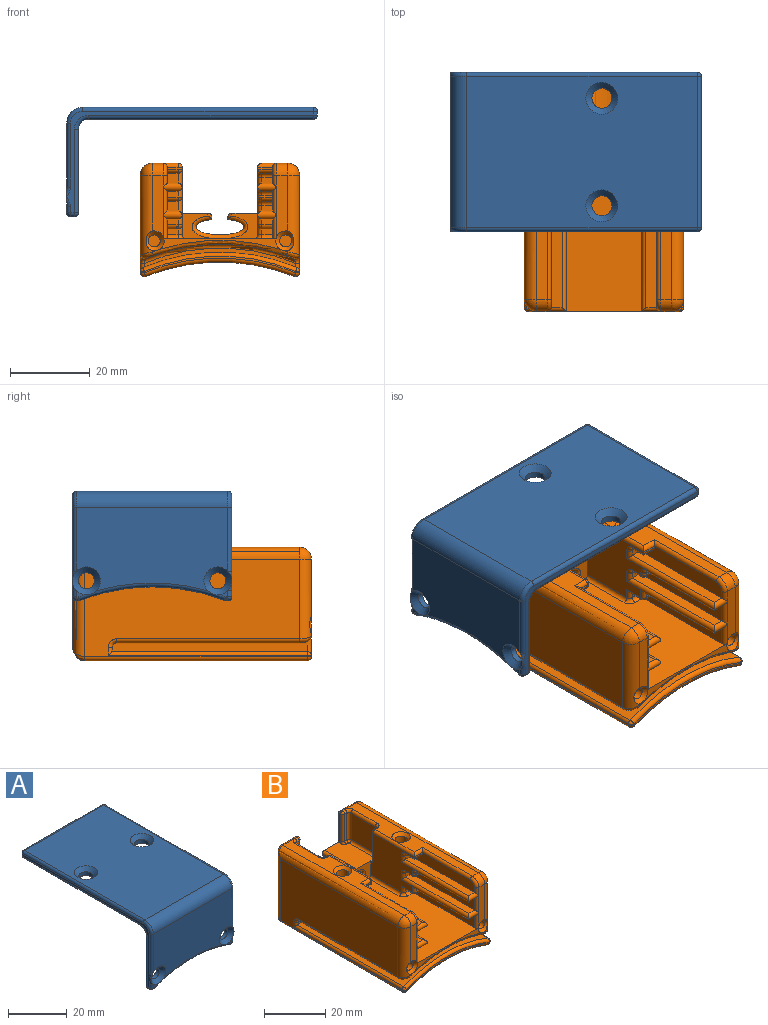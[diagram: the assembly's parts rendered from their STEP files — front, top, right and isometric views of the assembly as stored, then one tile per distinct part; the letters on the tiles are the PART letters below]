
ASSEMBLY  parts=2 mates=1
PART A: 66 faces, bbox 40.9x63.5x28 mm
  f0: plane 1.91x1.55mm, normal (0,-1,0), area 1.3mm2, adj f6,f26,f34,f58
  f1: plane 38x20.96mm, normal (0,-1,0), area 696.7mm2, adj f16,f25,f26,f29,f44,f58
  f2: plane 1.91x1.55mm, normal (0,-1,0), area 1.3mm2, adj f3,f25,f49,f58
  f3: cylinder r=1mm len=1mm, axis (-1,0,0), area 0.7mm2, adj f2,f7,f51,f59
  f4: plane 1x0.43mm, normal (0,0,-1), area 0.4mm2, adj f6,f8,f38,f62
  f5: cylinder r=1mm len=1mm, axis (-1,0,0), area 0.7mm2, adj f7,f9,f55,f63
  f6: cylinder r=1mm len=1mm, axis (-1,0,0), area 0.7mm2, adj f0,f4,f36,f60
  f7: plane 1x0.43mm, normal (0,0,-1), area 0.4mm2, adj f3,f5,f53,f61
  f8: cylinder r=1mm len=1mm, axis (-1,0,0), area 0.7mm2, adj f4,f9,f40,f64
  f9: plane 38x21mm, normal (0,1,0), area 685.6mm2, adj f5,f8,f10,f21,f22,f42,f57,f65
  f10: cylinder r=2.5mm len=38mm, axis (-1,0,0), area 149.2mm2, adj f9,f11,f41,f56
  f11: plane 56.5x38mm, normal (0,0,-1), area 2107.7mm2, adj f10,f12,f19,f20,f39,f54
  f12: cylinder r=1mm len=38mm, axis (-1,0,0), area 59.7mm2, adj f11,f13,f37,f52
  f13: plane 38x1mm, normal (0,1,0), area 38mm2, adj f12,f14,f35,f50
  f14: cylinder r=1mm len=38mm, axis (-1,0,0), area 59.7mm2, adj f13,f15,f33,f48
  f15: plane 58x38mm, normal (0,0,1), area 2103.5mm2, adj f14,f16,f23,f24,f31,f46
  f16: cylinder r=4mm len=38mm, axis (-1,0,0), area 238.8mm2, adj f1,f15,f30,f45
  f17: plane 62.13x25.63mm, normal (1,0,0), area 88mm2, adj f43,f44,f45,f46,f47,f49,f50,f53
  f18: plane 62.13x25.63mm, normal (-1,0,0), area 88mm2, adj f28,f29,f30,f31,f32,f34,f35,f38
  f19: cylinder r=2.5mm len=5mm, axis (0,0,1), area 23.6mm2, adj f11,f24
  f20: cylinder r=2.5mm len=5mm, axis (0,0,1), area 23.6mm2, adj f11,f23
  f21: cylinder r=2mm len=4mm, axis (0,1,0), area 18.8mm2, adj f9,f26
  f22: cylinder r=2mm len=4mm, axis (0,1,0), area 18.8mm2, adj f9,f25
  f23: cone r=2.5mm half-angle=45deg, axis (0,0,1), area 43.3mm2, adj f15,f20
  f24: cone r=2.5mm half-angle=45deg, axis (0,0,1), area 43.3mm2, adj f15,f19
  f25: cone r=3.5mm half-angle=45deg, axis (0,-1,0), area 36.7mm2, adj f1,f2,f22,f43,f47,f58
  f26: cone r=3.5mm half-angle=45deg, axis (0,-1,0), area 36.7mm2, adj f0,f1,f21,f28,f32,f58
  f27: cylinder r=50mm len=36.41mm, axis (0,-1,0), area 37.3mm2, adj f58,f61,f62,f65
  f28: bspline ~2.56x1.07mm, area 1.7mm2, adj f18,f26,f29
  f29: cylinder r=1mm len=16.05mm, axis (0,0,-1), area 25.2mm2, adj f1,f18,f28,f30
  f30: torus R=3mm, axis (1,0,0), area 9mm2, adj f16,f18,f29,f31
  f31: cylinder r=1mm len=58mm, axis (0,-1,0), area 91.1mm2, adj f15,f18,f30,f33
  f32: bspline ~2.56x1.07mm, area 1.7mm2, adj f18,f26,f34
  f33: sphere r=1mm, area 1.6mm2, adj f14,f31,f35
  f34: cylinder r=1mm len=1.55mm, axis (0,0,-1), area 2.4mm2, adj f0,f18,f32,f36
  f35: cylinder r=1mm len=1mm, axis (0,0,1), area 1.6mm2, adj f13,f18,f33,f37
  f36: sphere r=1mm, area 1.6mm2, adj f6,f34,f38
  f37: sphere r=1mm, area 1.6mm2, adj f12,f35,f39
  f38: cylinder r=1mm len=1mm, axis (0,1,0), area 1.6mm2, adj f4,f18,f36,f40
  f39: cylinder r=1mm len=56.5mm, axis (0,1,0), area 88.7mm2, adj f11,f18,f37,f41
  f40: sphere r=1mm, area 1.6mm2, adj f8,f38,f42
  f41: torus R=3.5mm, axis (1,0,0), area 7.1mm2, adj f10,f18,f39,f42
  f42: cylinder r=1mm len=21mm, axis (0,0,1), area 33mm2, adj f9,f18,f40,f41
  f43: bspline ~2.56x1.07mm, area 1.7mm2, adj f17,f25,f44
  f44: cylinder r=1mm len=16.05mm, axis (0,0,1), area 25.2mm2, adj f1,f17,f43,f45
  f45: torus R=3mm, axis (1,0,0), area 9mm2, adj f16,f17,f44,f46
  f46: cylinder r=1mm len=58mm, axis (0,1,0), area 91.1mm2, adj f15,f17,f45,f48
  f47: bspline ~2.56x1.07mm, area 1.7mm2, adj f17,f25,f49
  f48: sphere r=1mm, area 1.6mm2, adj f14,f46,f50
  f49: cylinder r=1mm len=1.55mm, axis (0,0,1), area 2.4mm2, adj f2,f17,f47,f51
  f50: cylinder r=1mm len=1mm, axis (0,0,-1), area 1.6mm2, adj f13,f17,f48,f52
  f51: sphere r=1mm, area 1.6mm2, adj f3,f49,f53
  f52: sphere r=1mm, area 1.6mm2, adj f12,f50,f54
  f53: cylinder r=1mm len=1mm, axis (0,-1,0), area 1.6mm2, adj f7,f17,f51,f55
  f54: cylinder r=1mm len=56.5mm, axis (0,-1,0), area 88.7mm2, adj f11,f17,f52,f56
  f55: sphere r=1mm, area 1.6mm2, adj f5,f53,f57
  f56: torus R=3.5mm, axis (1,0,0), area 7.1mm2, adj f10,f17,f54,f57
  f57: cylinder r=1mm len=21mm, axis (0,0,-1), area 33mm2, adj f9,f17,f55,f56
  f58: torus R=51mm, axis (0,1,0), area 57.3mm2, adj f0,f1,f2,f25,f26,f27,f59,f60
  f59: sphere r=1mm, area 0.4mm2, adj f3,f58,f61
  f60: sphere r=1mm, area 0.4mm2, adj f6,f58,f62
  f61: cylinder r=1mm len=1mm, axis (0,-1,0), area 0.4mm2, adj f7,f27,f59,f63
  f62: cylinder r=1mm len=1mm, axis (0,-1,0), area 0.4mm2, adj f4,f27,f60,f64
  f63: sphere r=1mm, area 0.4mm2, adj f5,f61,f65
  f64: sphere r=1mm, area 0.4mm2, adj f8,f62,f65
  f65: torus R=51mm, axis (0,-1,0), area 59mm2, adj f9,f27,f63,f64
PART B: 210 faces, bbox 44.8x60.6x29.6 mm
  f0: plane 15.41x2.75mm, normal (0,-1,0), area 39.4mm2, adj f65,f66,f122,f135,f139,f196
  f1: plane 30.46x2.65mm, normal (0,-1,0), area 28.4mm2, adj f43,f98,f196,f197
  f2: plane 0.74x0.29mm, normal (0,-1,0), area 0.1mm2, adj f73,f98,f197
  f3: plane 0.74x0.29mm, normal (0,-1,0), area 0.1mm2, adj f66,f98,f196
  f4: plane 9.5x6.5mm, normal (0,-1,0), area 26mm2, adj f5,f43,f52,f141,f187,f188
  f5: plane 16.37x8.87mm, normal (0,0,1), area 122.3mm2, adj f4,f6,f52,f55,f58,f142,f148,f161
  f6: plane 34x23.63mm, normal (0,1,0), area 451.1mm2, adj f5,f58,f59,f61,f69,f70,f71,f102
  f7: plane 9.5x6.5mm, normal (0,-1,0), area 26mm2, adj f43,f51,f61,f100,f186,f187
  f8: plane 56x6.5mm, normal (0,0,1), area 206.2mm2, adj f65,f68,f102,f105,f108,f112,f114,f123
  f9: plane 56x6.5mm, normal (0,0,1), area 206.2mm2, adj f72,f75,f146,f149,f153,f155,f162,f174
  f10: plane 4x2.75mm, normal (0,0,-1), area 11mm2, adj f15,f34,f124,f130
  f11: plane 4x2.75mm, normal (0,0,-1), area 11mm2, adj f17,f38,f118,f119
  f12: plane 4x2.75mm, normal (0,0,-1), area 11mm2, adj f18,f42,f110,f111
  f13: plane 15.41x2.75mm, normal (0,-1,0), area 39.4mm2, adj f73,f75,f163,f178,f184,f197
  f14: plane 29x2.75mm, normal (0,0,1), area 79.7mm2, adj f15,f34,f134,f137
  f15: plane 2.75x2.5mm, normal (0,-1,0), area 6.9mm2, adj f10,f14,f34,f133
  f16: plane 29x2.75mm, normal (0,0,1), area 79.7mm2, adj f17,f38,f121,f128
  f17: plane 2.75x2.5mm, normal (0,-1,0), area 6.9mm2, adj f11,f16,f38,f120
  f18: plane 2.75x1.5mm, normal (0,-1,0), area 4.1mm2, adj f12,f42,f101,f107
  f19: plane 24x2.75mm, normal (0,0,-1), area 66mm2, adj f20,f42,f121,f128
  f20: plane 2.75x1.5mm, normal (0,-1,0), area 4.1mm2, adj f19,f42,f111,f116
  f21: plane 24x2.75mm, normal (0,0,-1), area 66mm2, adj f22,f38,f134,f137
  f22: plane 2.75x1.5mm, normal (0,-1,0), area 4.1mm2, adj f21,f38,f119,f131
  f23: plane 2.75x0.5mm, normal (0,-1,0), area 1.4mm2, adj f34,f124,f125,f132
  f24: plane 3x2.75mm, normal (0,0,-1), area 8.3mm2, adj f36,f167,f172,f173
  f25: plane 3x2.75mm, normal (0,0,-1), area 8.3mm2, adj f40,f157,f159,f160
  f26: plane 4x2.75mm, normal (0,0,-1), area 11mm2, adj f44,f45,f150,f151
  f27: plane 56x24.5mm, normal (1,0,0), area 1124.7mm2, adj f71,f72,f73,f80,f85,f90,f92,f95
  f28: plane 38x4.17mm, normal (0,-1,0), area 17mm2, adj f81,f82,f85,f86
  f29: plane 56x24.5mm, normal (-1,0,0), area 1124.7mm2, adj f66,f68,f69,f77,f82,f87,f89,f91
  f30: cylinder r=50mm len=56mm, axis (0,1,0), area 2137.8mm2, adj f70,f77,f80,f81
  f31: cylinder r=50mm len=49.08mm, axis (0,-1,0), area 1951.2mm2, adj f33,f86,f87,f89,f90,f92
  f32: cylinder r=50mm len=48mm, axis (0,-1,0), area 1802.3mm2, adj f93,f94,f96,f97,f98,f99,f190,f191
  f33: plane 38x4.75mm, normal (0,-1,0), area 37mm2, adj f31,f89,f92,f93
  f34: plane 29x4mm, normal (1,0,0), area 107.9mm2, adj f10,f14,f15,f23,f124,f136,f138,f139
  f35: plane 29x2.75mm, normal (0,0,1), area 79.7mm2, adj f36,f37,f179,f182
  f36: plane 29x4mm, normal (-1,0,0), area 107.6mm2, adj f24,f35,f37,f50,f167,f173,f181,f183
  f37: plane 2.75x1.5mm, normal (0,-1,0), area 4.1mm2, adj f35,f36,f173,f180
  f38: plane 29x5mm, normal (1,0,0), area 132.7mm2, adj f11,f16,f17,f21,f22,f119,f135
  f39: plane 29x2.75mm, normal (0,0,1), area 79.7mm2, adj f40,f41,f164,f169
  f40: plane 29x5mm, normal (-1,0,0), area 132.3mm2, adj f25,f39,f41,f48,f49,f157,f159,f170
  f41: plane 2.75x1.5mm, normal (0,-1,0), area 4.1mm2, adj f39,f40,f157,f165
  f42: plane 29x5mm, normal (1,0,0), area 132.5mm2, adj f12,f18,f19,f20,f43,f101,f111,f122
  f43: plane 45x28.14mm, normal (0,0,1), area 1042.6mm2, adj f1,f4,f7,f42,f44,f100,f101,f104
  f44: plane 29x5mm, normal (-1,0,0), area 132.5mm2, adj f26,f43,f45,f46,f47,f140,f150,f163
  f45: plane 2.75x1.5mm, normal (0,-1,0), area 4.1mm2, adj f26,f44,f140,f147
  f46: plane 24x2.75mm, normal (0,0,-1), area 66mm2, adj f44,f47,f164,f169
  f47: plane 2.75x1.5mm, normal (0,-1,0), area 4.1mm2, adj f44,f46,f150,f156
  f48: plane 23x2.75mm, normal (0,0,-1), area 63.2mm2, adj f40,f170,f179,f182
  f49: plane 2.75x0.5mm, normal (0,-1,0), area 1.4mm2, adj f40,f159,f170,f171
  f50: plane 3.75x0.5mm, normal (0,-1,0), area 1.9mm2, adj f36,f52,f167,f177
  f51: plane 19x17mm, normal (1,0,0), area 254mm2, adj f7,f61,f100,f107,f110,f115,f116,f118
  f52: plane 21x17mm, normal (-1,0,0), area 257.1mm2, adj f4,f5,f50,f141,f147,f151,f156,f158
  f53: plane 11.5x1mm, normal (0,1,0), area 11.5mm2, adj f61,f109,f114,f115
  f54: plane 11x10.5mm, normal (1,0,0), area 115.5mm2, adj f103,f106,f108,f109
  f55: plane 11.5x1mm, normal (0,1,0), area 11.5mm2, adj f5,f152,f161,f162
  f56: plane 11x10.5mm, normal (-1,0,0), area 115.5mm2, adj f145,f148,f152,f153
  f57: plane 10.5x1mm, normal (0,-1,0), area 10.5mm2, adj f142,f145,f146,f202
  f58: plane 11.5x1.27mm, normal (-1,0,0), area 11.6mm2, adj f5,f6,f200,f202,f204
  f59: plane 11.5x1mm, normal (1,0,0), area 11.5mm2, adj f6,f61,f205,f208
  f60: plane 11.5x1mm, normal (0,-1,0), area 11.5mm2, adj f61,f102,f103,f205
  f61: plane 16x8.5mm, normal (0,0,1), area 123.9mm2, adj f6,f7,f51,f53,f59,f60,f106,f115
  f62: plane 13.97x0.67mm, normal (1,0,0), area 8.4mm2, adj f64,f185,f186,f209
  f63: plane 13.97x0.67mm, normal (-1,0,0), area 8.4mm2, adj f64,f188,f189,f209
  f64: extruded ~13x12mm, area 295.3mm2, adj f62,f63,f187,f209
  f65: cylinder r=3mm len=3mm, axis (1,0,0), area 13mm2, adj f0,f8,f67,f138
  f66: cylinder r=3mm len=20mm, axis (0,0,1), area 86.9mm2, adj f0,f3,f29,f67,f96,f196
  f67: sphere r=3mm, area 14.1mm2, adj f65,f66,f68
  f68: cylinder r=3mm len=56mm, axis (0,-1,0), area 259.2mm2, adj f8,f29,f67,f206
  f69: cylinder r=3mm len=26.5mm, axis (0,0,-1), area 113.4mm2, adj f6,f29,f76,f206
  f70: torus R=53mm, axis (0,-1,0), area 170.4mm2, adj f6,f30,f76,f78
  f71: cylinder r=3mm len=26.5mm, axis (0,0,1), area 113.4mm2, adj f6,f27,f78,f201
  f72: cylinder r=3mm len=56mm, axis (0,1,0), area 259.2mm2, adj f9,f27,f74,f201
  f73: cylinder r=3mm len=20mm, axis (0,0,-1), area 86.9mm2, adj f2,f13,f27,f74,f99,f197
  f74: sphere r=3mm, area 14.1mm2, adj f72,f73,f75
  f75: cylinder r=3mm len=3mm, axis (1,0,0), area 13mm2, adj f9,f13,f74,f183
  f76: bspline ~4.35x3.66mm, area 4.7mm2, adj f69,f70,f77
  f77: cylinder r=1mm len=56mm, axis (0,1,0), area 109.3mm2, adj f29,f30,f76,f79
  f78: bspline ~4.35x3.66mm, area 4.7mm2, adj f70,f71,f80
  f79: sphere r=1mm, area 2mm2, adj f77,f81,f82
  f80: cylinder r=1mm len=56mm, axis (0,1,0), area 109.3mm2, adj f27,f30,f78,f83
  f81: torus R=51mm, axis (0,-1,0), area 60.4mm2, adj f28,f30,f79,f83
  f82: cylinder r=1mm len=1mm, axis (0,0,1), area 0.5mm2, adj f28,f29,f79,f84
  f83: sphere r=1mm, area 2mm2, adj f80,f81,f85
  f84: sphere r=1mm, area 0.8mm2, adj f82,f86,f87
  f85: cylinder r=1mm len=1mm, axis (0,0,-1), area 0.5mm2, adj f27,f28,f83,f88
  f86: torus R=49mm, axis (0,-1,0), area 62.1mm2, adj f28,f31,f84,f88
  f87: cylinder r=1mm len=50mm, axis (0,-1,0), area 58.1mm2, adj f29,f31,f84,f89
  f88: sphere r=1mm, area 1.2mm2, adj f85,f86,f90
  f89: cylinder r=1mm len=2mm, axis (0,0,1), area 2.2mm2, adj f29,f31,f33,f87,f91
  f90: cylinder r=1mm len=50mm, axis (0,-1,0), area 58.1mm2, adj f27,f31,f88,f92
  f91: bspline ~2.7x2.14mm, area 4mm2, adj f29,f89,f93,f94
  f92: cylinder r=1mm len=2mm, axis (0,0,-1), area 2.2mm2, adj f27,f31,f33,f90,f95
  f93: torus R=49mm, axis (0,-1,0), area 60.8mm2, adj f32,f33,f91,f95
  f94: cylinder r=1mm len=46mm, axis (0,-1,0), area 89.8mm2, adj f29,f32,f91,f96
  f95: bspline ~2.42x2.41mm, area 4mm2, adj f27,f92,f93,f97
  f96: bspline ~3.98x3.78mm, area 7.8mm2, adj f32,f66,f94,f98
  f97: cylinder r=1mm len=46mm, axis (0,-1,0), area 89.8mm2, adj f27,f32,f95,f99
  f98: torus R=51mm, axis (0,-1,0), area 53.7mm2, adj f1,f2,f3,f32,f96,f99,f196,f197
  f99: bspline ~3.98x3.79mm, area 7.8mm2, adj f32,f73,f97,f98
  f100: cylinder r=1mm len=14mm, axis (0,-1,0), area 22mm2, adj f7,f43,f51,f104
  f101: cylinder r=1mm len=2.75mm, axis (1,0,0), area 4.3mm2, adj f18,f42,f43,f104
  f102: cylinder r=1mm len=7.5mm, axis (1,0,0), area 12.6mm2, adj f6,f8,f60,f105,f206,f207,f208
  f103: cylinder r=1mm len=11.5mm, axis (0,0,1), area 17.3mm2, adj f54,f60,f105,f106
  f104: torus R=2mm, axis (0,0,-1), area 3.4mm2, adj f43,f100,f101,f107
  f105: torus R=2mm, axis (0,0,1), area 3.4mm2, adj f8,f102,f103,f108
  f106: cylinder r=1mm len=13mm, axis (0,-1,0), area 18.8mm2, adj f54,f61,f103,f109
  f107: cylinder r=1mm len=2.5mm, axis (0,0,1), area 3.1mm2, adj f18,f51,f104,f110
  f108: cylinder r=1mm len=11mm, axis (0,1,0), area 17.3mm2, adj f8,f54,f105,f112
  f109: cylinder r=1mm len=11.5mm, axis (0,0,-1), area 17.3mm2, adj f53,f54,f106,f112
  f110: cylinder r=1mm len=5mm, axis (0,-1,0), area 7.1mm2, adj f12,f51,f107,f113
  f111: cylinder r=1mm len=2.75mm, axis (-1,0,0), area 4.3mm2, adj f12,f20,f42,f113
  f112: torus R=2mm, axis (0,0,1), area 3.4mm2, adj f8,f108,f109,f114
  f113: sphere r=1mm, area 2.1mm2, adj f110,f111,f116
  f114: cylinder r=1mm len=1mm, axis (-1,0,0), area 1.6mm2, adj f8,f53,f112,f117
  f115: cylinder r=1mm len=11.5mm, axis (0,0,-1), area 18.1mm2, adj f51,f53,f61,f117
  f116: cylinder r=1mm len=2.5mm, axis (0,0,1), area 3.1mm2, adj f20,f51,f113,f121
  f117: sphere r=1mm, area 1mm2, adj f114,f115,f123
  f118: cylinder r=1mm len=5mm, axis (0,-1,0), area 7.1mm2, adj f11,f51,f120,f127
  f119: cylinder r=1mm len=2.75mm, axis (-1,0,0), area 4.3mm2, adj f11,f22,f38,f127
  f120: cylinder r=1mm len=4.5mm, axis (0,0,1), area 5.5mm2, adj f17,f51,f118,f121
  f121: cylinder r=1mm len=31mm, axis (0,-1,0), area 86.8mm2, adj f16,f19,f51,f116,f120,f128
  f122: cylinder r=1mm len=6mm, axis (0,0,1), area 8.6mm2, adj f0,f42,f43,f128,f196
  f123: cylinder r=1mm len=18mm, axis (0,-1,0), area 28.3mm2, adj f8,f51,f117,f129
  f124: cylinder r=1mm len=2.75mm, axis (-1,0,0), area 4.3mm2, adj f10,f23,f34,f126
  f125: cylinder r=1mm len=1mm, axis (0,0,1), area 0.8mm2, adj f23,f51,f126,f129
  f126: sphere r=1mm, area 1.6mm2, adj f124,f125,f130
  f127: sphere r=1mm, area 1.6mm2, adj f118,f119,f131
  f128: cylinder r=1mm len=4.75mm, axis (1,0,0), area 12.2mm2, adj f16,f19,f121,f122,f135
  f129: sphere r=1mm, area 1.6mm2, adj f123,f125,f132
  f130: cylinder r=1mm len=5mm, axis (0,-1,0), area 7.1mm2, adj f10,f51,f126,f133
  f131: cylinder r=1mm len=2.5mm, axis (0,0,1), area 3.1mm2, adj f22,f51,f127,f134
  f132: cylinder r=1mm len=3.75mm, axis (1,0,0), area 5.1mm2, adj f8,f23,f129,f136
  f133: cylinder r=1mm len=4.5mm, axis (0,0,1), area 5.5mm2, adj f15,f51,f130,f134
  f134: cylinder r=1mm len=31mm, axis (0,-1,0), area 86.8mm2, adj f14,f21,f51,f131,f133,f137
  f135: cylinder r=1mm len=7mm, axis (0,0,1), area 9.4mm2, adj f0,f38,f128,f137
  f136: cylinder r=1mm len=23mm, axis (0,1,0), area 35.3mm2, adj f8,f34,f132,f138
  f137: cylinder r=1mm len=4.75mm, axis (1,0,0), area 12.2mm2, adj f14,f21,f134,f135,f139
  f138: torus R=2mm, axis (-1,0,0), area 6.5mm2, adj f34,f65,f136,f139
  f139: cylinder r=1mm len=3mm, axis (0,0,1), area 3.9mm2, adj f0,f34,f137,f138
  f140: cylinder r=1mm len=2.75mm, axis (1,0,0), area 4.3mm2, adj f43,f44,f45,f143
  f141: cylinder r=1mm len=14mm, axis (0,1,0), area 22mm2, adj f4,f43,f52,f143
  f142: cylinder r=1mm len=1mm, axis (-1,0,0), area 1.6mm2, adj f5,f57,f144,f200
  f143: torus R=2mm, axis (0,0,-1), area 3.4mm2, adj f43,f140,f141,f147
  f144: sphere r=1mm, area 1mm2, adj f142,f145,f148
  f145: cylinder r=1mm len=10.5mm, axis (0,0,-1), area 16.5mm2, adj f56,f57,f144,f149
  f146: cylinder r=1mm len=7.5mm, axis (1,0,0), area 12.6mm2, adj f6,f9,f57,f149,f201,f203,f204
  f147: cylinder r=1mm len=2.5mm, axis (0,0,-1), area 3.1mm2, adj f45,f52,f143,f151
  f148: cylinder r=1mm len=12mm, axis (0,1,0), area 18.1mm2, adj f5,f56,f144,f152
  f149: torus R=2mm, axis (0,0,1), area 3.4mm2, adj f9,f145,f146,f153
  f150: cylinder r=1mm len=2.75mm, axis (-1,0,0), area 4.3mm2, adj f26,f44,f47,f154
  f151: cylinder r=1mm len=5mm, axis (0,1,0), area 7.1mm2, adj f26,f52,f147,f154
  f152: cylinder r=1mm len=11.5mm, axis (0,0,1), area 17.3mm2, adj f55,f56,f148,f155
  f153: cylinder r=1mm len=11mm, axis (0,-1,0), area 17.3mm2, adj f9,f56,f149,f155
  f154: sphere r=1mm, area 1.6mm2, adj f150,f151,f156
  f155: torus R=2mm, axis (0,0,1), area 3.4mm2, adj f9,f152,f153,f162
  f156: cylinder r=1mm len=2.5mm, axis (0,0,-1), area 3.1mm2, adj f47,f52,f154,f164
  f157: cylinder r=1mm len=2.75mm, axis (-1,0,0), area 4.3mm2, adj f25,f40,f41,f158
  f158: torus R=2mm, axis (1,0,0), area 3.4mm2, adj f52,f157,f160,f165
  f159: cylinder r=1mm len=2.75mm, axis (-1,0,0), area 4.3mm2, adj f25,f40,f49,f166
  f160: cylinder r=1mm len=3mm, axis (0,1,0), area 4.7mm2, adj f25,f52,f158,f166
  f161: cylinder r=1mm len=11.5mm, axis (0,0,1), area 18.1mm2, adj f5,f52,f55,f168
  f162: cylinder r=1mm len=1mm, axis (-1,0,0), area 1.6mm2, adj f9,f55,f155,f168
  f163: cylinder r=1mm len=6mm, axis (0,0,-1), area 8.6mm2, adj f13,f43,f44,f169,f197
  f164: cylinder r=1mm len=31mm, axis (0,1,0), area 86.8mm2, adj f39,f46,f52,f156,f165,f169
  f165: cylinder r=1mm len=2.5mm, axis (0,0,-1), area 3.1mm2, adj f41,f52,f158,f164
  f166: sphere r=1mm, area 1.6mm2, adj f159,f160,f171
  f167: cylinder r=1mm len=3.75mm, axis (-1,0,0), area 5.1mm2, adj f24,f36,f50,f172
  f168: sphere r=1mm, area 2.1mm2, adj f161,f162,f174
  f169: cylinder r=1mm len=4.75mm, axis (1,0,0), area 12.2mm2, adj f39,f46,f163,f164,f178
  f170: cylinder r=1mm len=2.75mm, axis (-1,0,0), area 4.3mm2, adj f40,f48,f49,f175
  f171: cylinder r=1mm len=1mm, axis (0,0,-1), area 0.8mm2, adj f49,f52,f166,f175
  f172: cylinder r=1mm len=4mm, axis (0,1,0), area 5.5mm2, adj f24,f52,f167,f176
  f173: cylinder r=1mm len=2.75mm, axis (-1,0,0), area 4.3mm2, adj f24,f36,f37,f176
  f174: cylinder r=1mm len=19mm, axis (0,1,0), area 29.1mm2, adj f9,f52,f168,f177
  f175: torus R=2mm, axis (1,0,0), area 3.4mm2, adj f52,f170,f171,f179
  f176: torus R=2mm, axis (1,0,0), area 3.4mm2, adj f52,f172,f173,f180
  f177: cylinder r=1mm len=4.75mm, axis (1,0,0), area 5.9mm2, adj f9,f50,f174,f181
  f178: cylinder r=1mm len=7mm, axis (0,0,-1), area 9.4mm2, adj f13,f40,f169,f182
  f179: cylinder r=1mm len=31mm, axis (0,1,0), area 84.5mm2, adj f35,f48,f52,f175,f180,f182
  f180: cylinder r=1mm len=2.5mm, axis (0,0,-1), area 3.1mm2, adj f37,f52,f176,f179
  f181: cylinder r=1mm len=23mm, axis (0,-1,0), area 35.3mm2, adj f9,f36,f177,f183
  f182: cylinder r=1mm len=4.75mm, axis (1,0,0), area 12.2mm2, adj f35,f48,f178,f179,f184
  f183: torus R=2mm, axis (-1,0,0), area 6.5mm2, adj f36,f75,f181,f184
  f184: cylinder r=1mm len=3mm, axis (0,0,-1), area 3.9mm2, adj f13,f36,f182,f183
  f185: cylinder r=1mm len=15mm, axis (0,-1,0), area 23mm2, adj f6,f61,f62,f186,f209
  f186: cylinder r=1mm len=1.61mm, axis (0,0,1), area 1.1mm2, adj f7,f62,f185,f187
  f187: bspline ~14.01x6mm, area 37.8mm2, adj f4,f7,f64,f186,f188
  f188: cylinder r=1mm len=1.61mm, axis (0,0,-1), area 1.1mm2, adj f4,f63,f187,f189
  f189: cylinder r=1mm len=15mm, axis (0,-1,0), area 23mm2, adj f5,f6,f63,f188,f209
  f190: cylinder r=2mm len=20.67mm, axis (0,0,1), area 259.7mm2, adj f32,f199
  f191: cylinder r=2mm len=21.79mm, axis (0,0,1), area 273.8mm2, adj f32,f198
  f192: cylinder r=1.5mm len=29mm, axis (0,-1,0), area 273.3mm2, adj f193,f197
  f193: plane 3x3mm, normal (0,-1,0), area 7.1mm2, adj f192
  f194: cylinder r=1.5mm len=29mm, axis (0,-1,0), area 273.3mm2, adj f195,f196
  f195: plane 3x3mm, normal (0,-1,0), area 7.1mm2, adj f194
  f196: cone r=1.5mm half-angle=45deg, axis (0,-1,0), area 15.6mm2, adj f0,f1,f3,f43,f66,f98,f122,f194
  f197: cone r=1.5mm half-angle=45deg, axis (0,-1,0), area 15.6mm2, adj f1,f2,f13,f43,f73,f98,f163,f192
  f198: cone r=2mm half-angle=45deg, axis (0,0,1), area 22.2mm2, adj f9,f191
  f199: cone r=2mm half-angle=45deg, axis (0,0,1), area 22.2mm2, adj f8,f190
  f200: torus R=2mm, axis (-1,0,0), area 2.1mm2, adj f5,f58,f142,f202
  f201: bspline ~3.13x3mm, area 3.2mm2, adj f71,f72,f146
  f202: cylinder r=1mm len=10.5mm, axis (0,0,1), area 16.5mm2, adj f57,f58,f200,f203
  f203: sphere r=1mm, area 1.6mm2, adj f146,f202,f204
  f204: cylinder r=1mm len=1mm, axis (0,-1,0), area 0.8mm2, adj f58,f146,f203
  f205: cylinder r=1mm len=11.5mm, axis (0,0,1), area 18.1mm2, adj f59,f60,f61,f207
  f206: bspline ~3.13x3mm, area 3.2mm2, adj f68,f69,f102
  f207: sphere r=1mm, area 1.6mm2, adj f102,f205,f208
  f208: cylinder r=1mm len=1mm, axis (0,1,0), area 0.8mm2, adj f59,f102,f207
  f209: bspline ~14.01x6mm, area 39.3mm2, adj f6,f62,f63,f64,f185,f189
PLACE A rot(axis=(0,0,-1),90deg) t=(53.96,9.4,-47.35)mm
PLACE B rot(axis=(0,0,-1),0deg) t=(39.47,9.4,-22.9)mm
MATE parallel B.f6 <-> A.f18  axis (0,1,0) through (39.47,9.4,-22.16)mm
